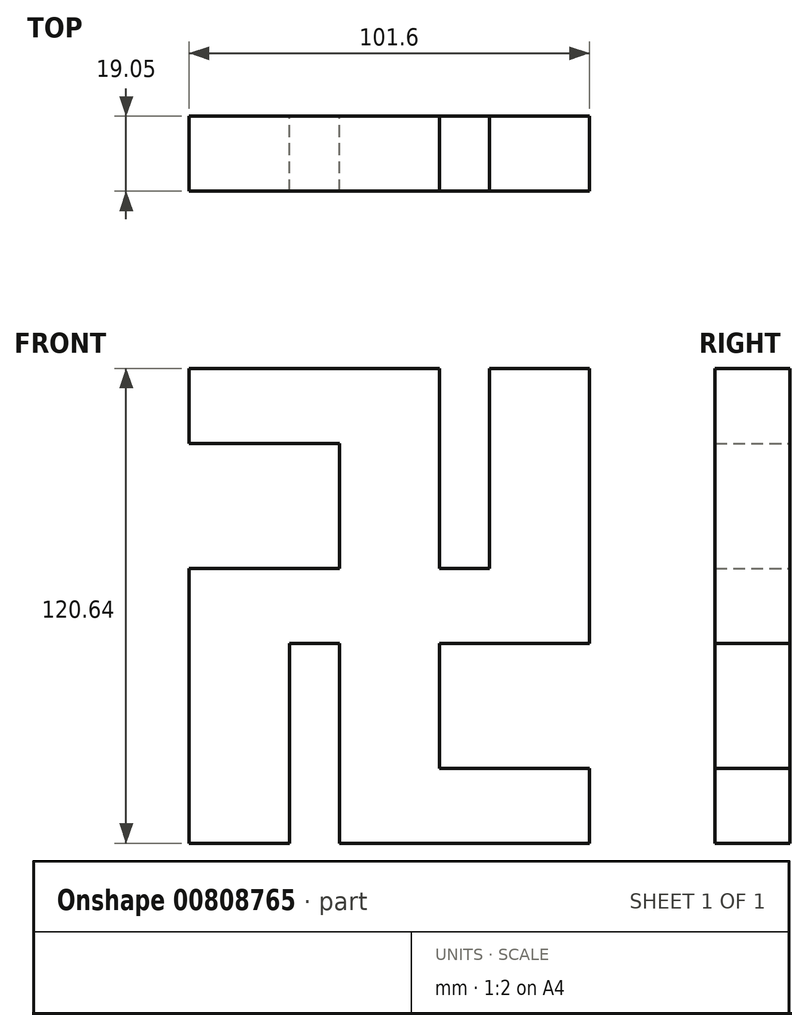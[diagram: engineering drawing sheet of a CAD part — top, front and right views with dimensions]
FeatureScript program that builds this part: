
annotation { "Feature Type Name" : "Feature", "Feature Type Description" : "" }
export const myFeature = defineFeature(function(context is Context, id is Id, definition is map)
    precondition{}
    {
        {
            var Q0;
            Q0=qCreatedBy(makeId("Front.planeOp"),FACE);
            var sketch = newSketch(context, id + "F0", { "sketchPlane" : qUnion([Q0])});
            skLineSegment(sketch, "E0.bottom", {"start": v(50.8, -9.52) * mm, "end": v(-50.8, -9.53) * mm});
            skLineSegment(sketch, "E0.top", {"start": v(50.8, 9.53) * mm, "end": v(-50.8, 9.52) * mm});
            skLineSegment(sketch, "E0.left", {"start": v(50.8, -9.52) * mm, "end": v(50.8, 9.53) * mm});
            skLineSegment(sketch, "E0.right", {"start": v(-50.8, -9.53) * mm, "end": v(-50.8, 9.52) * mm});
            skPoint(sketch, "E0.middle", {"position": v(0, 0) * mm});
            skLineSegment(sketch, "E1", {"start": v(0, 0) * mm, "end": v(0, 9.53) * mm});
            skLineSegment(sketch, "E2", {"start": v(0, 9.53) * mm, "end": v(50.8, 9.53) * mm});
            skLineSegment(sketch, "E3", {"start": v(0, 9.53) * mm, "end": v(25.4, 9.53) * mm});
            skLineSegment(sketch, "E4", {"start": v(25.4, 9.53) * mm, "end": v(25.4, 60.33) * mm});
            skLineSegment(sketch, "E5", {"start": v(25.4, 60.33) * mm, "end": v(50.8, 60.33) * mm});
            skLineSegment(sketch, "E6", {"start": v(50.8, 60.33) * mm, "end": v(50.8, 9.53) * mm});
            skLineSegment(sketch, "E7", {"start": v(0, 0) * mm, "end": v(0, -9.53) * mm});
            skLineSegment(sketch, "E8", {"start": v(0, -9.53) * mm, "end": v(-50.8, -9.53) * mm});
            skLineSegment(sketch, "E9", {"start": v(0, -9.53) * mm, "end": v(-25.4, -9.53) * mm});
            skLineSegment(sketch, "E10", {"start": v(-50.8, -9.53) * mm, "end": v(-50.8, -60.33) * mm});
            skLineSegment(sketch, "E11", {"start": v(-25.4, -9.53) * mm, "end": v(-25.4, -60.33) * mm});
            skLineSegment(sketch, "E12", {"start": v(-25.4, -60.33) * mm, "end": v(-50.8, -60.33) * mm});
            skLineSegment(sketch, "E13", {"start": v(0, -9.53) * mm, "end": v(25.4, -9.52) * mm});
            skLineSegment(sketch, "E14", {"start": v(0, -9.53) * mm, "end": v(50.8, -9.52) * mm});
            skLineSegment(sketch, "E15", {"start": v(0, 9.53) * mm, "end": v(12.7, 9.53) * mm});
            skLineSegment(sketch, "E16", {"start": v(0, 9.52) * mm, "end": v(-12.7, 9.52) * mm});
            skLineSegment(sketch, "E17", {"start": v(12.7, 9.53) * mm, "end": v(12.7, 60.33) * mm});
            skLineSegment(sketch, "E18", {"start": v(12.7, 60.33) * mm, "end": v(-12.7, 60.33) * mm});
            skLineSegment(sketch, "E19", {"start": v(-12.7, 9.52) * mm, "end": v(-12.7, 41.27) * mm});
            skLineSegment(sketch, "E20", {"start": v(-12.7, 41.27) * mm, "end": v(-50.8, 41.27) * mm});
            skLineSegment(sketch, "E21", {"start": v(-50.8, 41.27) * mm, "end": v(-50.8, 60.33) * mm});
            skLineSegment(sketch, "E22", {"start": v(-50.8, 60.33) * mm, "end": v(-12.7, 60.33) * mm});
            skLineSegment(sketch, "E23", {"start": v(0, -9.53) * mm, "end": v(-12.7, -9.53) * mm});
            skLineSegment(sketch, "E24", {"start": v(-12.7, -9.53) * mm, "end": v(-12.7, -60.33) * mm});
            skLineSegment(sketch, "E25", {"start": v(0, -9.53) * mm, "end": v(12.7, -9.53) * mm});
            skLineSegment(sketch, "E26", {"start": v(12.7, -9.53) * mm, "end": v(12.7, -41.27) * mm});
            skLineSegment(sketch, "E27", {"start": v(-12.7, -60.33) * mm, "end": v(50.8, -60.33) * mm});
            skLineSegment(sketch, "E28", {"start": v(50.8, -60.33) * mm, "end": v(50.8, -41.27) * mm});
            skLineSegment(sketch, "E29", {"start": v(12.7, -41.27) * mm, "end": v(50.8, -41.27) * mm});
            skSolve(sketch);
        }
        {
            var Q0;
            Q0 = qSketchRegion(id + "F0", true);
            extrude(context, id + "F1", {"entities" : qUnion([Q0]), "depth" : 19.05 * mm, "offsetDistance" : 25.4 * mm});
        }
    });
